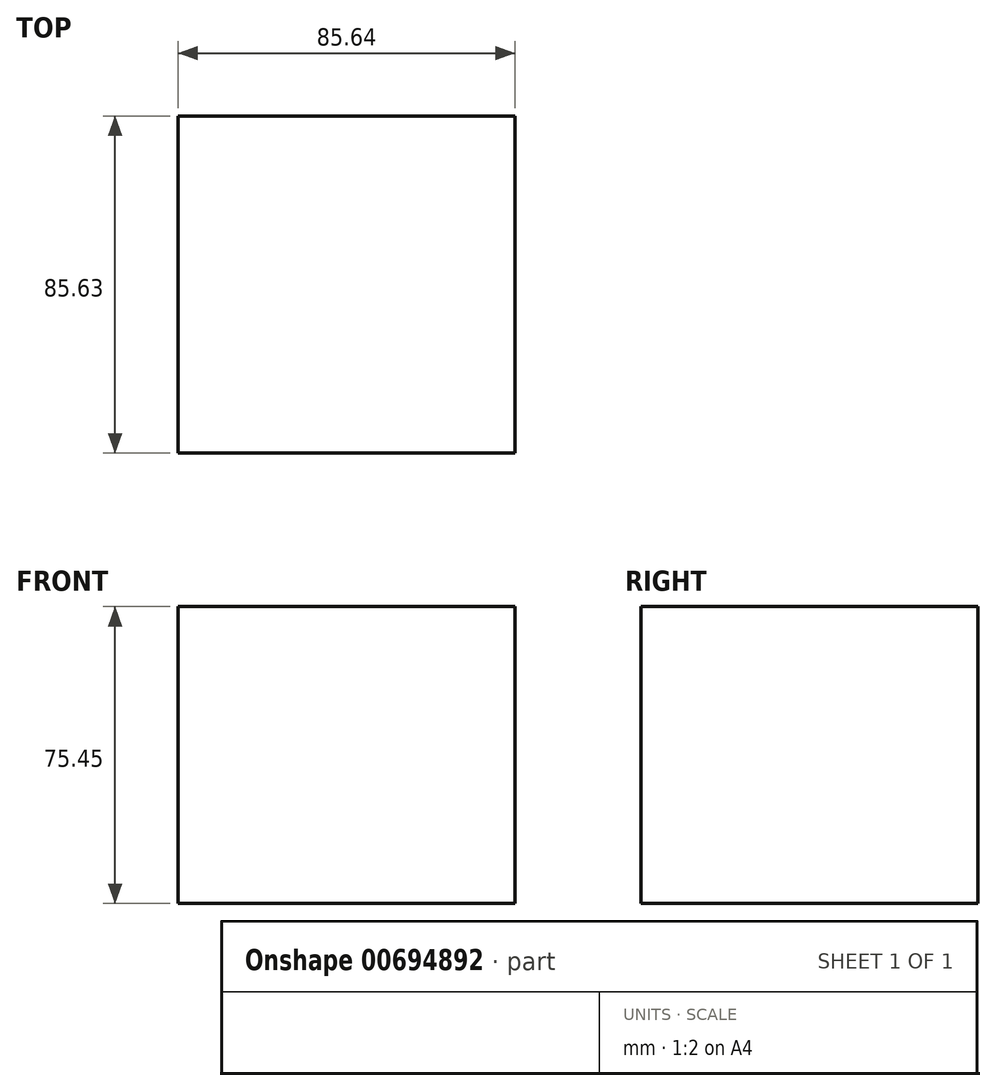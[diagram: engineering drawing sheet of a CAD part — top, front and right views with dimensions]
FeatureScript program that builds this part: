
annotation { "Feature Type Name" : "Feature", "Feature Type Description" : "" }
export const myFeature = defineFeature(function(context is Context, id is Id, definition is map)
    precondition{}
    {
        {
            var Q0;
            Q0=qCreatedBy(makeId("Front.planeOp"),FACE);
            var sketch = newSketch(context, id + "F0", { "sketchPlane" : qUnion([Q0])});
            skLineSegment(sketch, "E0.bottom", {"start": v(-43.37, 36.76) * mm, "end": v(42.27, 36.76) * mm});
            skLineSegment(sketch, "E0.top", {"start": v(-43.37, -38.69) * mm, "end": v(42.27, -38.69) * mm});
            skLineSegment(sketch, "E0.left", {"start": v(-43.37, 36.76) * mm, "end": v(-43.37, -38.69) * mm});
            skLineSegment(sketch, "E0.right", {"start": v(42.27, 36.76) * mm, "end": v(42.27, -38.69) * mm});
            skSolve(sketch);
        }
        {
            var Q0;
            Q0=makeQuery(id+"F0.imprint","IMPRINT",FACE,{"disambiguationData":[TD([[makeQuery(id+"F0.imprint","IMPRINT",EDGE,{"derivedFrom":sQuery(id+"F0.wireOp",EDGE,"E0.bottom")}),-1.0]])]});
            extrude(context, id + "F1", {"entities" : qUnion([Q0]), "depth" : 85.63 * mm, "offsetDistance" : 25 * mm});
        }
    });
